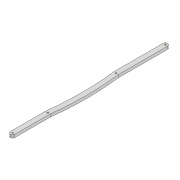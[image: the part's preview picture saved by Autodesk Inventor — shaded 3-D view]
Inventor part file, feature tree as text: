
AUTODESK INVENTOR PART (.ipt)
format: ipt  version: 2022 (Build 260153000, 153)  size: 102,912 bytes
history: native  units: mm
features: extrude x1, other x1, sketch x1
ambient origin geometry x8: Origin, YZ Plane, XZ Plane, XY Plane, X Axis, Y Axis, Z Axis, Center Point
bodies: Solid1 (feature_tree)
feature tree (3):
  extrude  "Extrusion1"  Depth=600.0mm
  other  "Work Axis3"
  sketch  "Sketch1"  dims[d0=3.3mm d1=3.3mm d2=10.0mm d3=322.934mm d4=3.3mm d5=74.182mm d6=6.0mm d7=0.0mm d8=3.3mm d9=218.733mm d12=600.0mm d13=600.0mm]
